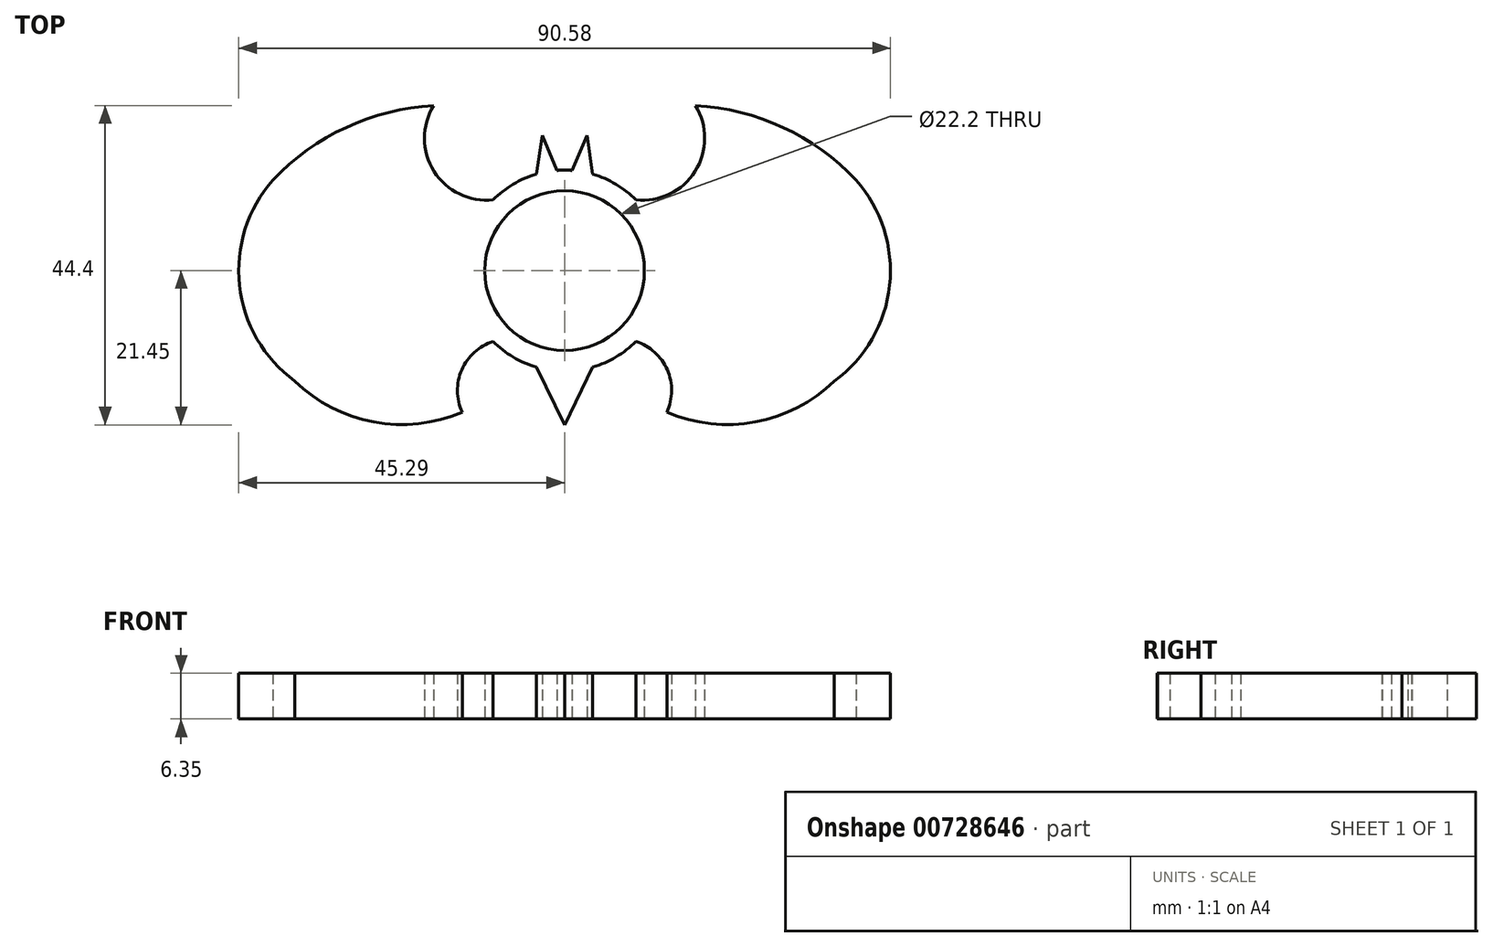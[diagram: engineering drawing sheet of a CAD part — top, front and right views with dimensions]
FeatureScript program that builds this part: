
annotation { "Feature Type Name" : "Feature", "Feature Type Description" : "" }
export const myFeature = defineFeature(function(context is Context, id is Id, definition is map)
    precondition{}
    {
        {
            var Q0;
            Q0=qCreatedBy(makeId("Top.planeOp"),FACE);
            var sketch = newSketch(context, id + "F0", { "sketchPlane" : qUnion([Q0])});
            skCircle(sketch, "E0", {"center": v(0, 0) * mm, "radius": 13.97 * mm});
            skLineSegment(sketch, "E1", {"start": v(0, 0) * mm, "end": v(-26.24, 0) * mm});
            skLineSegment(sketch, "E2", {"start": v(0, 0) * mm, "end": v(26.24, 0) * mm});
            skArc(sketch, "E3", {"start": v(37.5, -15.37) * mm, "mid": v(45.18, -2.05) * mm, "end": v(40.53, 12.6) * mm});
            skArc(sketch, "E4", {"start": v(-18.2, 22.95) * mm, "mid": v(-30.36, 19.9) * mm, "end": v(-40.53, 12.6) * mm});
            skArc(sketch, "E5", {"start": v(-18.2, 22.95) * mm, "mid": v(-18.15, 13.81) * mm, "end": v(-9.93, 9.83) * mm});
            skArc(sketch, "E6.trimOffspring", {"start": v(-40.53, 12.6) * mm, "mid": v(-45.18, -2.05) * mm, "end": v(-37.5, -15.37) * mm});
            skArc(sketch, "E7.MirrorCS", {"start": v(18.2, 22.95) * mm, "mid": v(18.15, 13.81) * mm, "end": v(9.93, 9.83) * mm});
            skArc(sketch, "E8.MirrorCS", {"start": v(18.2, 22.95) * mm, "mid": v(30.36, 19.9) * mm, "end": v(40.53, 12.6) * mm});
            skArc(sketch, "E9", {"start": v(-37.5, -15.37) * mm, "mid": v(-26.51, -21.03) * mm, "end": v(-14.22, -19.66) * mm});
            skArc(sketch, "E10", {"start": v(-9.93, -9.83) * mm, "mid": v(-14.29, -13.78) * mm, "end": v(-14.22, -19.66) * mm});
            skArc(sketch, "E11.MirrorCS", {"start": v(9.93, -9.83) * mm, "mid": v(14.29, -13.78) * mm, "end": v(14.22, -19.66) * mm});
            skArc(sketch, "E12.MirrorCS", {"start": v(37.5, -15.37) * mm, "mid": v(26.51, -21.03) * mm, "end": v(14.22, -19.66) * mm});
            skPoint(sketch, "E13.end.orphan", {"position": v(2.34, 18.82) * mm});
            skPoint(sketch, "E14.orphan", {"position": v(3.92, 13.4) * mm});
            skPoint(sketch, "E15.end.orphan", {"position": v(-1.04, 13.93) * mm});
            skPoint(sketch, "E16.end.orphan", {"position": v(-2.23, 18.82) * mm});
            skPoint(sketch, "E17.MirrorCS.end.orphan", {"position": v(1.04, 13.93) * mm});
            skPoint(sketch, "E17.MirrorCS.start.orphan", {"position": v(2.23, 18.82) * mm});
            skPoint(sketch, "E18.end.orphan", {"position": v(-4.8, 18.35) * mm});
            skPoint(sketch, "E19.MirrorCS.end.orphan", {"position": v(4.8, 18.35) * mm});
            skLineSegment(sketch, "E20", {"start": v(-1.04, 13.93) * mm, "end": v(-3.1, 18.83) * mm});
            skLineSegment(sketch, "E21", {"start": v(-3.1, 18.83) * mm, "end": v(-3.92, 13.4) * mm});
            skLineSegment(sketch, "E22.MirrorCS", {"start": v(1.04, 13.93) * mm, "end": v(3.1, 18.83) * mm});
            skLineSegment(sketch, "E23.MirrorCS", {"start": v(3.1, 18.83) * mm, "end": v(3.92, 13.4) * mm});
            skPoint(sketch, "E24.end.orphan", {"position": v(0, -21.45) * mm});
            skPoint(sketch, "E24.start.orphan", {"position": v(-4.01, -13.38) * mm});
            skPoint(sketch, "E25.MirrorCS.start.orphan", {"position": v(4.01, -13.38) * mm});
            skPoint(sketch, "E26.MirrorCS.end.orphan", {"position": v(-3.92, -13.4) * mm});
            skPoint(sketch, "E26.MirrorCS.start.orphan", {"position": v(-3.1, -18.83) * mm});
            skLineSegment(sketch, "E27", {"start": v(-3.92, -13.4) * mm, "end": v(0, -21.45) * mm});
            skLineSegment(sketch, "E28.MirrorCS", {"start": v(3.92, -13.4) * mm, "end": v(0, -21.45) * mm});
            skCircle(sketch, "E29", {"center": v(0, 0) * mm, "radius": 11.1 * mm});
            skSolve(sketch);
        }
        {
            var Q0;
            Q0=qSketchRegion(id+"F0",true);
            extrude(context, id + "F1", {"entities" : qUnion([Q0]), "depth" : 6.35 * mm, "offsetDistance" : 25.4 * mm});
        }
    });
